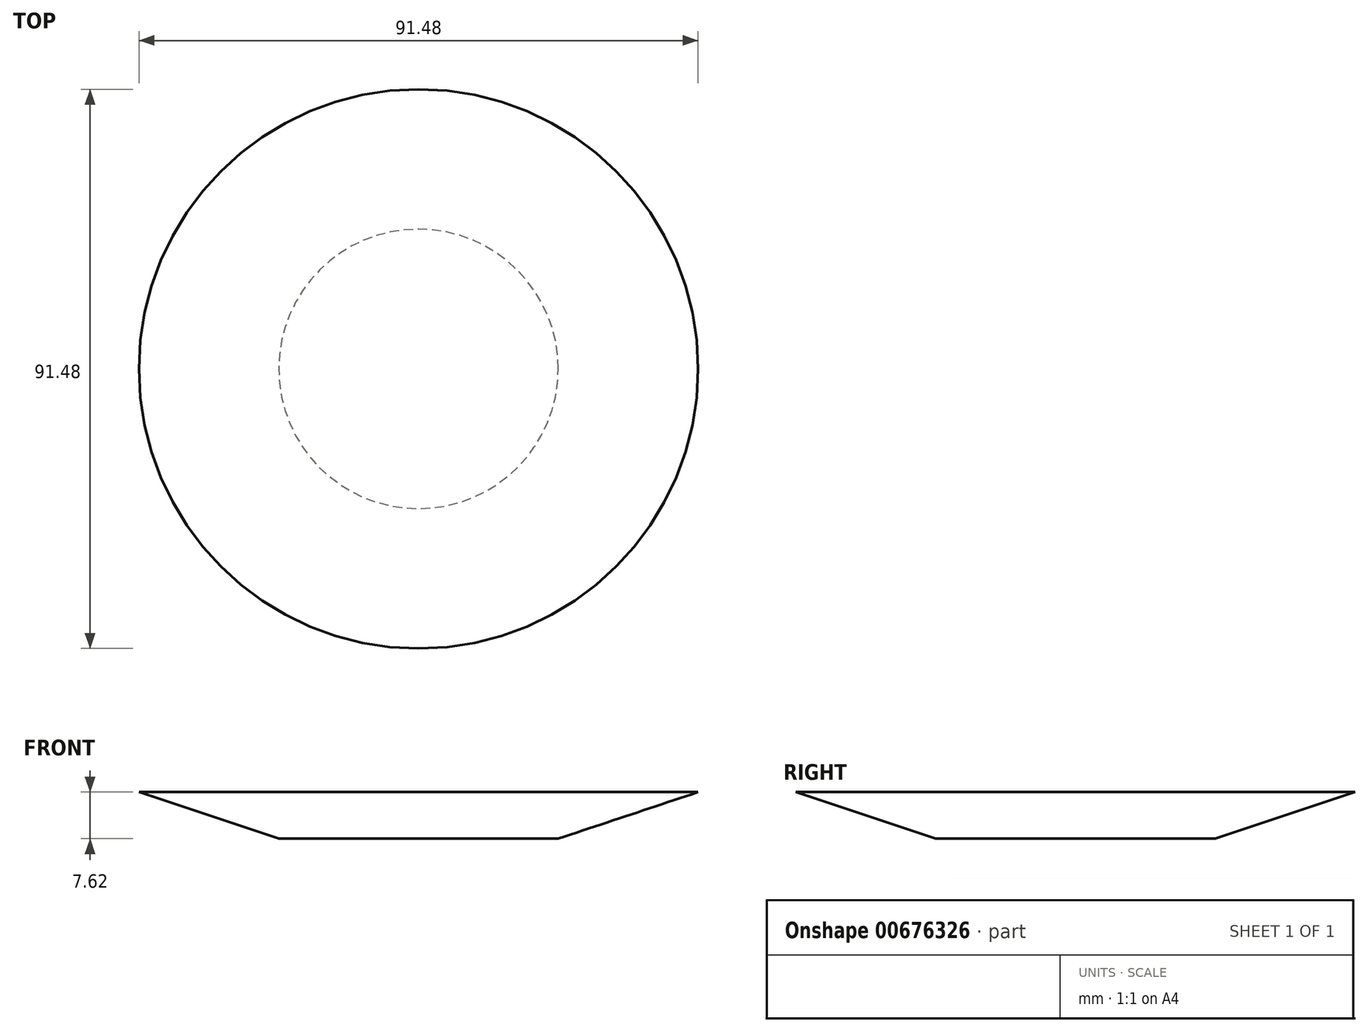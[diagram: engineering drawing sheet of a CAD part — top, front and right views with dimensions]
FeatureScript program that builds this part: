
annotation { "Feature Type Name" : "Feature", "Feature Type Description" : "" }
export const myFeature = defineFeature(function(context is Context, id is Id, definition is map)
    precondition{}
    {
        {
            var Q0;
            Q0=qCreatedBy(makeId("Front.planeOp"),FACE);
            var sketch = newSketch(context, id + "F0", { "sketchPlane" : qUnion([Q0])});
            skLineSegment(sketch, "E0", {"start": v(10.16, 11.28) * mm, "end": v(0, 11.28) * mm, "construction": true});
            skArc(sketch, "E1", {"start": v(2.95, 21.66) * mm, "mid": v(1.49, 21.97) * mm, "end": v(0, 22.07) * mm});
            skLineSegment(sketch, "E2", {"start": v(0, 22.07) * mm, "end": v(0, -16.03) * mm});
            skLineSegment(sketch, "E3", {"start": v(0, -16.03) * mm, "end": v(38.12, -16.03) * mm});
            skLineSegment(sketch, "E4", {"start": v(0, -16.03) * mm, "end": v(0, -23.65) * mm});
            skLineSegment(sketch, "E5", {"start": v(0, -23.65) * mm, "end": v(22.86, -23.65) * mm});
            skLineSegment(sketch, "E6", {"start": v(38.12, -16.03) * mm, "end": v(45.74, -16.03) * mm});
            skLineSegment(sketch, "E7", {"start": v(45.74, -16.03) * mm, "end": v(22.86, -23.65) * mm});
            skFitSpline(sketch, "E8", {"points": [v(45.74, -16.03) * mm, v(19.56, 7.12) * mm, v(6.17, 16.65) * mm, v(10.16, 11.28) * mm], "startDerivative": vector(-14.9, 8.81) * mm, "endDerivative": vector(1.96, 43.38) * mm});
            skSolve(sketch);
        }
        {
            var Q0;
            Q0=qSketchRegion(id+"F0",true);
            var Q1;
            Q1=sQuery(id+"F0.wireOp",EDGE,"E2");
            revolve(context, id + "F1", {"entities" : qUnion([Q0]), "axis" : qUnion([Q1]), "revolveType" : RevolveType.FULL});
        }
    });
